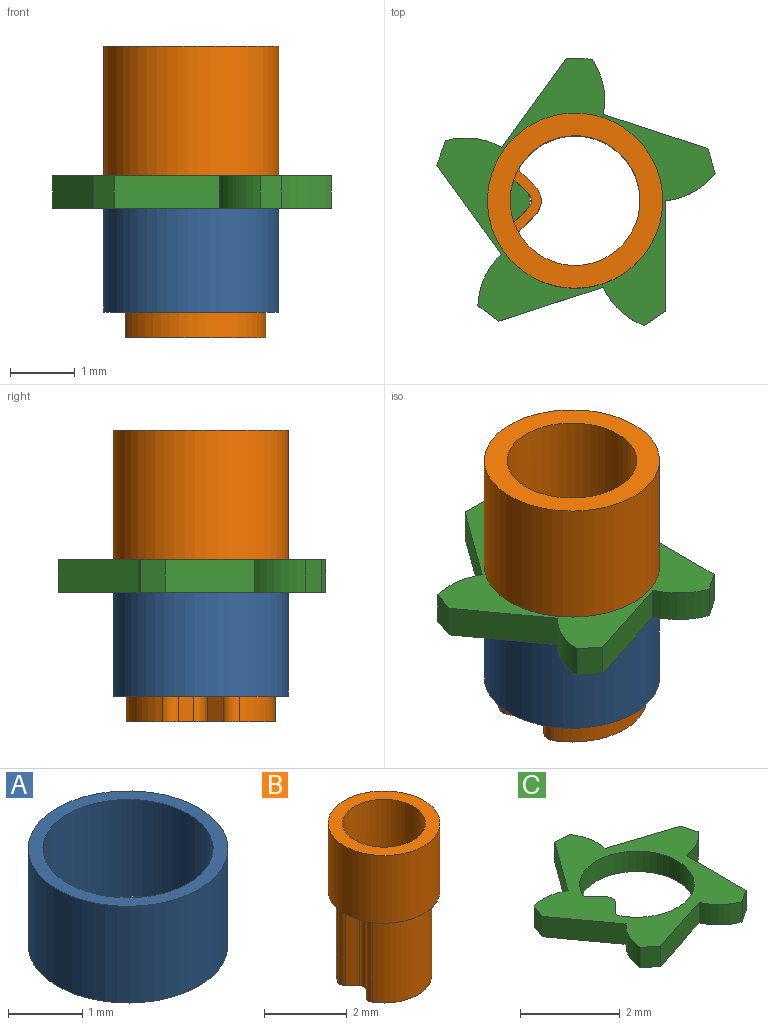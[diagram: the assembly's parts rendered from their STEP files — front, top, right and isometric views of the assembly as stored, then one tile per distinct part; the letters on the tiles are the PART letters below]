
ASSEMBLY  parts=3 mates=2
PART A: 4 faces, bbox 2.7x2.7x1.6 mm
  f0: cylinder r=1.15mm len=2.3mm, axis (0,0,-1), area 11.6mm2, adj f2,f3
  f1: cylinder r=1.35mm len=2.7mm, axis (0,0,-1), area 13.6mm2, adj f2,f3
  f2: plane 2.7x2.7mm, normal (0,0,1), area 1.6mm2, adj f0,f1
  f3: plane 2.7x2.7mm, normal (0,0,-1), area 1.6mm2, adj f0,f1
PART B: 17 faces, bbox 2.7x2.7x4.5 mm
  f0: plane 2.7x2.7mm, normal (0,0,-1), area 1.7mm2, adj f1,f2,f5,f6,f8,f9,f15
  f1: cylinder r=1mm len=4.5mm, axis (0,0,-1), area 25.6mm2, adj f0,f3,f4,f10,f11,f16
  f2: cylinder r=1.35mm len=2.7mm, axis (0,0,-1), area 17mm2, adj f0,f3
  f3: plane 2.7x2.7mm, normal (0,0,1), area 2.6mm2, adj f1,f2
  f4: plane 1.03x0.42mm, normal (0,0,1), area 0.2mm2, adj f1,f6,f7,f8,f10,f11,f12,f13
  f5: cylinder r=0.2mm len=2.5mm, axis (0,0,1), area 0.7mm2, adj f0,f6,f15,f16
  f6: plane 2.5x0.24mm, normal (-0.71,0.71,0), area 0.9mm2, adj f0,f4,f5,f7,f16
  f7: cylinder r=0.15mm len=2.5mm, axis (0,0,1), area 0.6mm2, adj f4,f6,f8,f16
  f8: plane 2.5x0.24mm, normal (-0.71,-0.71,0), area 0.9mm2, adj f0,f4,f7,f9,f16
  f9: cylinder r=0.2mm len=2.5mm, axis (0,0,1), area 0.7mm2, adj f0,f8,f15,f16
  f10: cylinder r=0.05mm len=2.5mm, axis (0,0,1), area 0.2mm2, adj f1,f4,f14,f16
  f11: cylinder r=0.05mm len=2.5mm, axis (0,0,1), area 0.2mm2, adj f1,f4,f12,f16
  f12: plane 2.5x0.24mm, normal (0.71,0.71,0), area 0.9mm2, adj f4,f11,f13,f16
  f13: cylinder r=0.3mm len=2.5mm, axis (0,0,1), area 1.2mm2, adj f4,f12,f14,f16
  f14: plane 2.5x0.24mm, normal (0.71,-0.71,0), area 0.9mm2, adj f4,f10,f13,f16
  f15: cylinder r=1.15mm len=2.5mm, axis (0,0,1), area 15mm2, adj f0,f5,f9,f16
  f16: plane 2.3x2.17mm, normal (0,0,-1), area 1mm2, adj f1,f5,f6,f7,f8,f9,f10,f11
PART C: 23 faces, bbox 4.3x4.1x0.5 mm
  f0: plane 0.5x0.26mm, normal (0.71,-0.71,0), area 0.2mm2, adj f1,f20,f21,f22
  f1: cylinder r=0.2mm len=0.5mm, axis (0,0,-1), area 0.2mm2, adj f0,f2,f21,f22
  f2: plane 0.5x0.26mm, normal (0.71,0.71,0), area 0.2mm2, adj f1,f3,f21,f22
  f3: cylinder r=0.1mm len=0.5mm, axis (0,0,-1), area 0.1mm2, adj f2,f4,f21,f22
  f4: cylinder r=1.15mm len=2.3mm, axis (0,0,-1), area 3.1mm2, adj f3,f20,f21,f22
  f5: plane 0.5x0.4mm, normal (0.03,1,0), area 0.2mm2, adj f6,f19,f21,f22
  f6: plane 1.37x1mm, normal (-0.81,0.59,0), area 0.8mm2, adj f5,f7,f21,f22
  f7: cylinder r=1.12mm len=0.86mm, axis (0,0,-1), area 0.4mm2, adj f6,f8,f21,f22
  f8: plane 0.5x0.38mm, normal (-0.94,0.34,0), area 0.2mm2, adj f7,f9,f21,f22
  f9: plane 1.37x1mm, normal (-0.81,-0.59,0), area 0.8mm2, adj f8,f10,f21,f22
  f10: cylinder r=1.12mm len=0.79mm, axis (0,0,-1), area 0.4mm2, adj f9,f11,f21,f22
  f11: plane 0.5x0.32mm, normal (-0.61,-0.79,0), area 0.2mm2, adj f10,f12,f21,f22
  f12: plane 1.61x0.52mm, normal (0.31,-0.95,0), area 0.8mm2, adj f11,f13,f21,f22
  f13: cylinder r=1.12mm len=0.64mm, axis (0,0,-1), area 0.4mm2, adj f12,f14,f21,f22
  f14: plane 0.5x0.33mm, normal (0.56,-0.83,0), area 0.2mm2, adj f13,f15,f21,f22
  f15: plane 1.7x0.5mm, normal (1,0,0), area 0.8mm2, adj f14,f16,f21,f22
  f16: cylinder r=1.12mm len=0.76mm, axis (0,0,-1), area 0.4mm2, adj f15,f17,f21,f22
  f17: plane 0.5x0.38mm, normal (0.96,0.28,0), area 0.2mm2, adj f16,f18,f21,f22
  f18: plane 1.61x0.52mm, normal (0.31,0.95,0), area 0.8mm2, adj f17,f19,f21,f22
  f19: cylinder r=1.12mm len=0.85mm, axis (0,0,-1), area 0.4mm2, adj f5,f18,f21,f22
  f20: cylinder r=0.1mm len=0.5mm, axis (0,0,-1), area 0.1mm2, adj f0,f4,f21,f22
  f21: plane 4.29x4.12mm, normal (0,0,1), area 6mm2, adj f0,f1,f2,f3,f4,f5,f6,f7
  f22: plane 4.29x4.12mm, normal (0,0,-1), area 6mm2, adj f0,f1,f2,f3,f4,f5,f6,f7
PLACE A t=(0,0,-2.1)mm
PLACE B at identity
PLACE C t=(0,0,-0.5)mm
MATE fastened C.f4 <-> A.f0  axis (0,0,-1) through (0,0,-0.5)mm
MATE fastened B.f1 <-> C.f4  axis (0,0,1) through (0,0,0)mm
